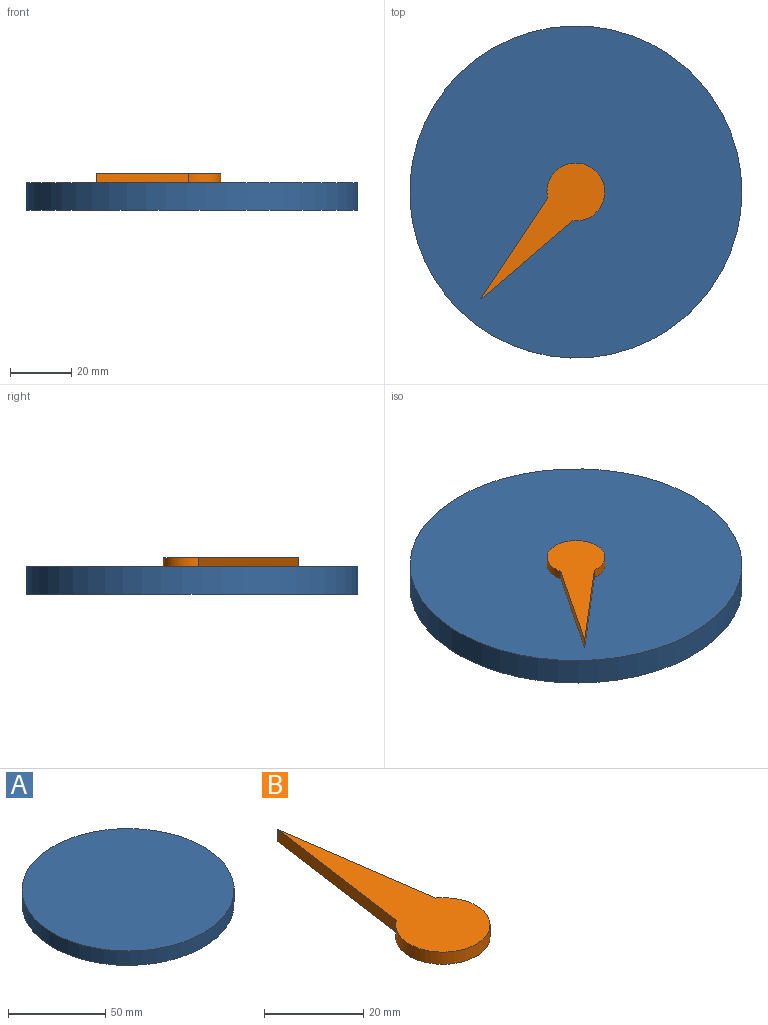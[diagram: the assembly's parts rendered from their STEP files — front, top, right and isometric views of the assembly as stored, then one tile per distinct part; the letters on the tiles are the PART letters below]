
ASSEMBLY  parts=2 mates=1
PART A: 3 faces, bbox 108.9x108.9x9 mm
  f0: cylinder r=54.44mm len=108.88mm, axis (0,0,-1), area 3078.5mm2, adj f1,f2
  f1: plane 108.88x108.88mm, normal (0,0,1), area 9310.8mm2, adj f0
  f2: plane 108.88x108.88mm, normal (0,0,-1), area 9310.8mm2, adj f0
PART B: 5 faces, bbox 19x56.4x3 mm
  f0: cylinder r=9.48mm len=18.97mm, axis (0,0,-1), area 143.4mm2, adj f1,f2,f3,f4
  f1: plane 39.16x5.51mm, normal (0.99,0.14,0), area 118.6mm2, adj f0,f2,f3,f4
  f2: plane 39.19x5.55mm, normal (-0.99,0.14,0), area 118.7mm2, adj f0,f1,f3,f4
  f3: plane 56.36x18.97mm, normal (0,0,1), area 485.7mm2, adj f0,f1,f2
  f4: plane 56.36x18.97mm, normal (0,0,-1), area 485.7mm2, adj f0,f1,f2
PLACE A at identity fixed
PLACE B rot(axis=(0,0,1),138.4deg) t=(0,0,0)mm
MATE revolute A.f0 <-> B.f0  axis (0,0,1) through (0,0,9)mm
